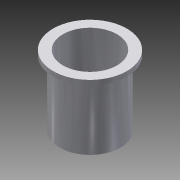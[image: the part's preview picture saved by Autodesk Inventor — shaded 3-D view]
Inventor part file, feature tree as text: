
AUTODESK INVENTOR PART (.ipt)
format: ipt  version: 2015 (Build 190159000, 159)  size: 126,976 bytes
history: native  units: in
note: dims shown in document units (in); Inventor stores cm internally (conversion verified against a paired STEP export)
features: revolve x1, sketch x1
ambient origin geometry x8: Origin, YZ Plane, XZ Plane, XY Plane, X Axis, Y Axis, Z Axis, Center Point
bodies: Solid1 (feature_tree)
feature tree (2):
  revolve  "Revolution1"  [1 undecoded]
  sketch  "Sketch1"  dims[d0=0.75in d1=1.0in d2=0.2185in d3=2.594in d4=0.5841in d5=0.5in d6=1.844in d7=0.5in d8=1.75in d9=0.25in d10=105.0deg d11=0.5in d12=0.5in d13=0.25in d14=0.375in d15=2.0in d16=0.5in d17=0.25in d18=0.234in d19=0.25in d20=2.0in d21=0.25in d22=105.0deg d23=0.125in d24=0.25in d25=2.3995in d26=0.125in d27=0.25in d28=180.0deg]
note: 1 required parameter value undecoded (feature->parameter linkage not recoverable at this tier; creation-order binding heuristic only, values carry confidence <= 0.55)
